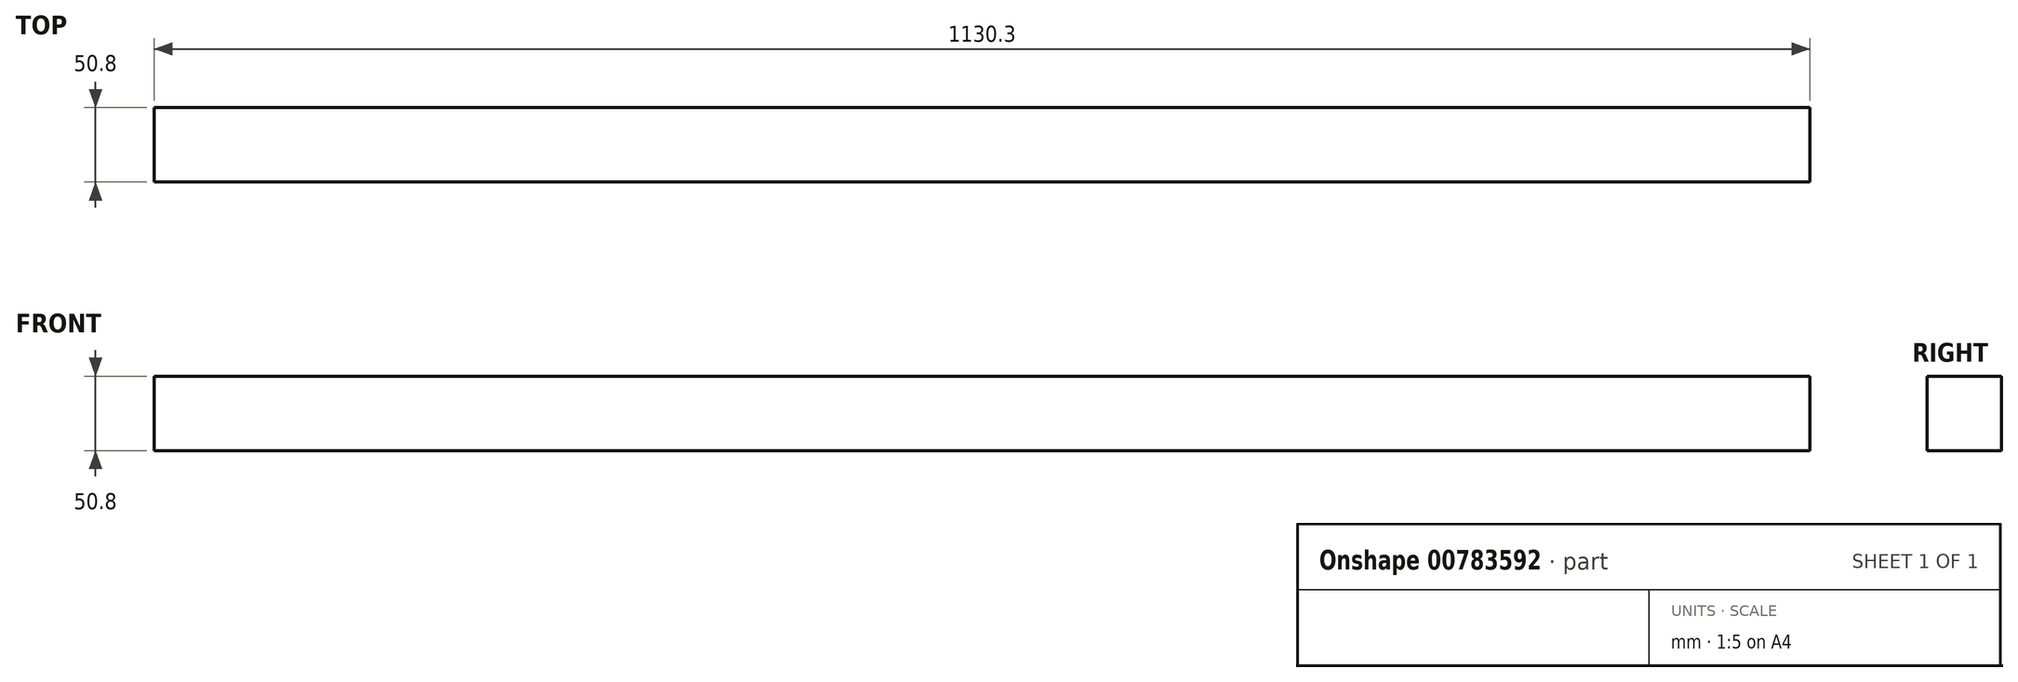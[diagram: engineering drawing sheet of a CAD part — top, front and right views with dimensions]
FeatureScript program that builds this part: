
annotation { "Feature Type Name" : "Feature", "Feature Type Description" : "" }
export const myFeature = defineFeature(function(context is Context, id is Id, definition is map)
    precondition{}
    {
        {
            var Q0;
            Q0=qCreatedBy(makeId("Front.planeOp"),FACE);
            var sketch = newSketch(context, id + "F0", { "sketchPlane" : qUnion([Q0])});
            skLineSegment(sketch, "E0.bottom", {"start": v(0, 0) * mm, "end": v(1130.3, 0) * mm});
            skLineSegment(sketch, "E0.top", {"start": v(0, 50.8) * mm, "end": v(1130.3, 50.8) * mm});
            skLineSegment(sketch, "E0.left", {"start": v(0, 0) * mm, "end": v(0, 50.8) * mm});
            skLineSegment(sketch, "E0.right", {"start": v(1130.3, 0) * mm, "end": v(1130.3, 50.8) * mm});
            skSolve(sketch);
        }
        {
            var Q0;
            Q0=makeQuery(id+"F0.imprint","IMPRINT",FACE,{"disambiguationData":[TD([[makeQuery(id+"F0.imprint","IMPRINT",EDGE,{"derivedFrom":sQuery(id+"F0.wireOp",EDGE,"E0.bottom")}),1.0]])]});
            extrude(context, id + "F1", {"entities" : qUnion([Q0]), "depth" : 50.8 * mm, "offsetDistance" : 25.4 * mm});
        }
    });
